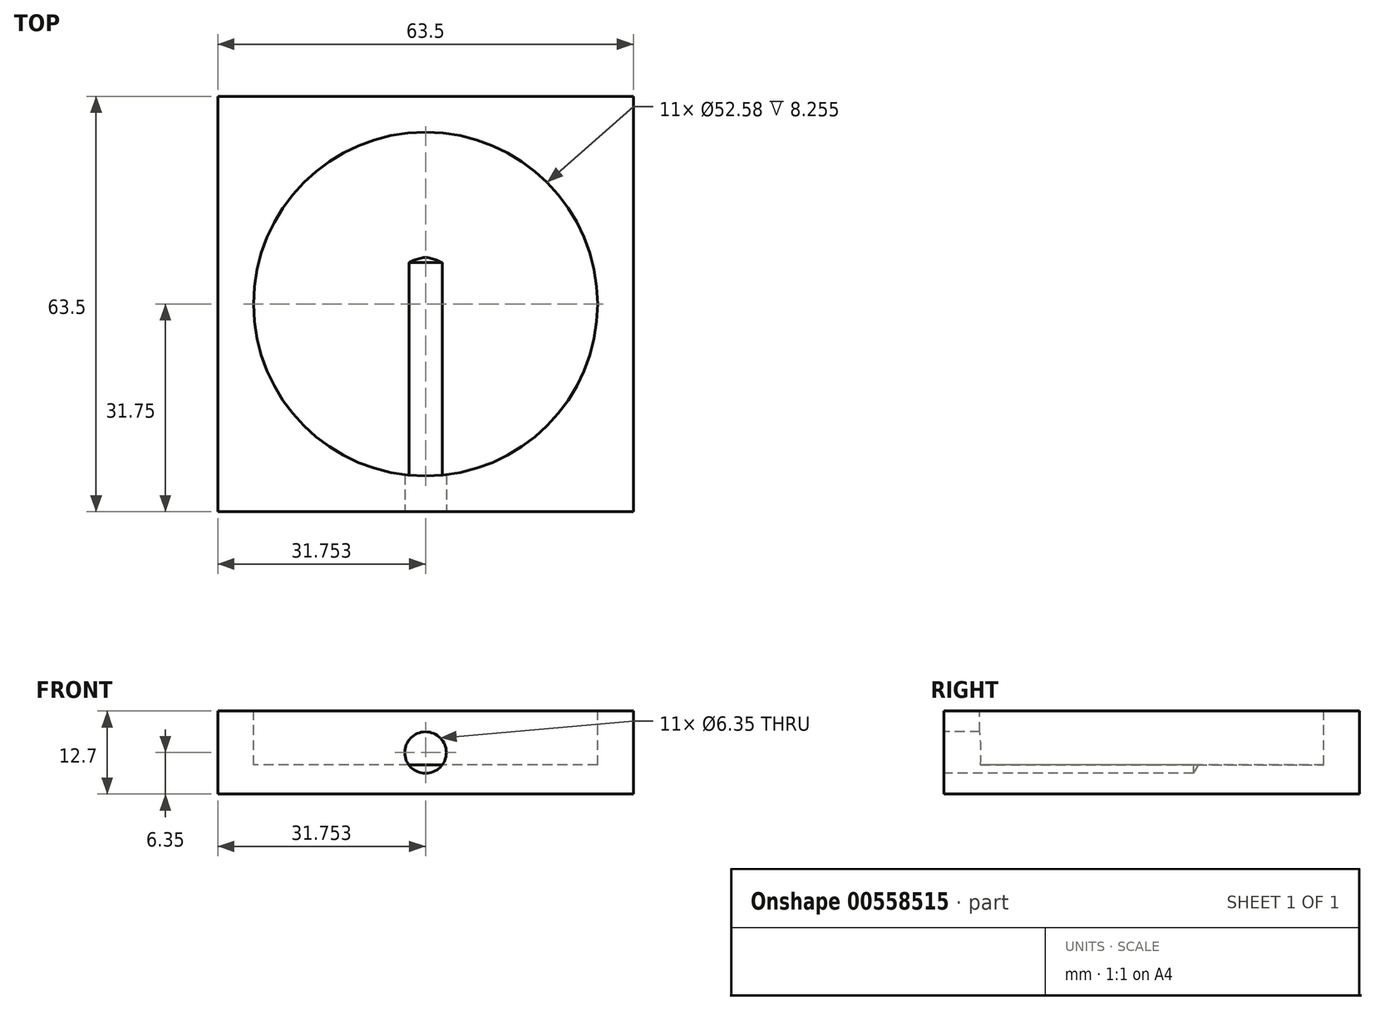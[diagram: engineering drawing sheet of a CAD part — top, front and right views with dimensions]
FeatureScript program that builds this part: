
annotation { "Feature Type Name" : "Feature", "Feature Type Description" : "" }
export const myFeature = defineFeature(function(context is Context, id is Id, definition is map)
    precondition{}
    {
        {
            var Q0;
            Q0=qCreatedBy(makeId("Front.planeOp"),FACE);
            var sketch = newSketch(context, id + "F0", { "sketchPlane" : qUnion([Q0])});
            skLineSegment(sketch, "E0.bottom", {"start": v(-56.1, 12.7) * mm, "end": v(7.4, 12.7) * mm});
            skLineSegment(sketch, "E0.top", {"start": v(-56.1, 0) * mm, "end": v(7.4, 0) * mm});
            skLineSegment(sketch, "E0.left", {"start": v(-56.1, 12.7) * mm, "end": v(-56.1, 0) * mm});
            skLineSegment(sketch, "E0.right", {"start": v(7.4, 12.7) * mm, "end": v(7.4, 0) * mm});
            skPoint(sketch, "E1", {"position": v(-30.7, 6.35) * mm});
            skSolve(sketch);
        }
        {
            var Q0;
            Q0 = qSketchRegion(id + "F0", true);
            extrude(context, id + "F1", {"entities" : qUnion([Q0]), "depth" : 63.5 * mm, "offsetDistance" : 25.4 * mm});
        }
        {
            var Q0;
            Q0=makeQuery(id+"F1.opExtrude","SWEPT_FACE",FACE,{"disambiguationData":[OSD([sQuery(id+"F0.wireOp",EDGE,"E0.bottom")])]});
            var sketch = newSketch(context, id + "F2", { "sketchPlane" : qUnion([Q0])});
            skPoint(sketch, "E2", {"position": v(-24.35, -31.75) * mm});
            skCircle(sketch, "E3", {"center": v(-24.35, -31.75) * mm, "radius": 26.29 * mm});
            skSolve(sketch);
        }
        {
            var Q0;
            Q0 = qSketchRegion(id + "F2", true);
            extrude(context, id + "F3", {"entities" : qUnion([Q0]), "operationType" : NewBodyOperationType.REMOVE, "oppositeDirection" : true, "depth" : 8.25 * mm, "offsetDistance" : 25.4 * mm});
        }
        {
            var Q0;
            Q0=makeQuery(id+"F1.opExtrude","CAP_FACE",FACE,{"disambiguationData":[OSD([sQuery(id+"F0.wireOp",EDGE,"E0.bottom"),sQuery(id+"F0.wireOp",EDGE,"E0.top"),sQuery(id+"F0.wireOp",EDGE,"E0.left"),sQuery(id+"F0.wireOp",EDGE,"E0.right")])],"isStart":false});
            var sketch = newSketch(context, id + "F4", { "sketchPlane" : qUnion([Q0])});
            skPoint(sketch, "E4", {"position": v(-24.35, 6.35) * mm});
            skSolve(sketch);
        }
        {
            var Q0;
            Q0=sQuery(id+"F4.wireOp",VERTEX,"E4");
            var Q1;
            Q1=makeQuery(id+"F1.opExtrude","SWEPT_BODY",BODY,{"disambiguationData":[OSD([sQuery(id+"F0.wireOp",EDGE,"E0.bottom"),sQuery(id+"F0.wireOp",EDGE,"E0.top"),sQuery(id+"F0.wireOp",EDGE,"E0.left"),sQuery(id+"F0.wireOp",EDGE,"E0.right")])]});
            hole(context, id + "F5", {"style" : HoleStyle.SIMPLE, "endStyle" : HoleEndStyle.BLIND, "holeDiameter" : 6.35 * mm, "holeDepth" : 38.1 * mm, "isTappedThrough" : true, "tappedDepth" : 12.7 * mm, "tapClearance" : 3, "locations" : qUnion([Q0]), "scope" : qUnion([Q1])});
        }
    });
